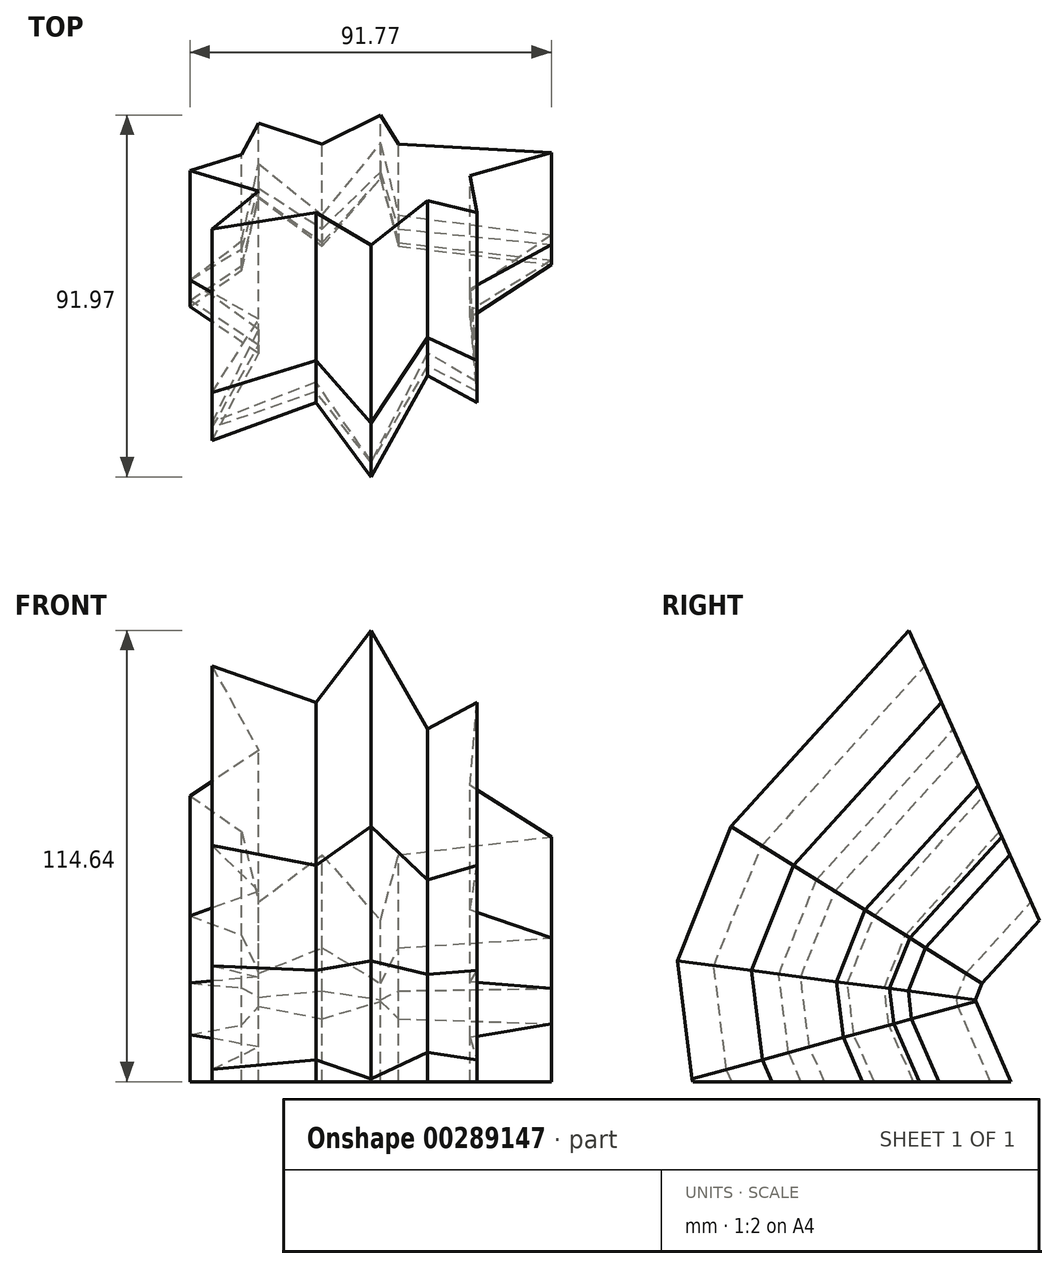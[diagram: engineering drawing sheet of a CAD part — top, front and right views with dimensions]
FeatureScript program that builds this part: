
annotation { "Feature Type Name" : "Feature", "Feature Type Description" : "" }
export const myFeature = defineFeature(function(context is Context, id is Id, definition is map)
    precondition{}
    {
        {
            var Q0;
            Q0=qCreatedBy(makeId("Top.planeOp"),FACE);
            var sketch = newSketch(context, id + "F0", { "sketchPlane" : qUnion([Q0])});
            skLineSegment(sketch, "E0", {"start": v(-44, 0) * mm, "end": v(-30.89, 9.97) * mm});
            skLineSegment(sketch, "E1", {"start": v(-30.89, 9.97) * mm, "end": v(-26.58, 29.54) * mm});
            skLineSegment(sketch, "E2", {"start": v(-26.58, 29.54) * mm, "end": v(-10.42, 16.43) * mm});
            skLineSegment(sketch, "E3", {"start": v(-10.42, 16.43) * mm, "end": v(4.37, 34.67) * mm});
            skLineSegment(sketch, "E4", {"start": v(4.37, 34.67) * mm, "end": v(8.98, 16.43) * mm});
            skLineSegment(sketch, "E5", {"start": v(8.98, 16.43) * mm, "end": v(47.77, 11.4) * mm});
            skLineSegment(sketch, "E6", {"start": v(47.77, 11.4) * mm, "end": v(27.12, -2.96) * mm});
            skLineSegment(sketch, "E7", {"start": v(27.12, -2.96) * mm, "end": v(28.91, -25.95) * mm});
            skLineSegment(sketch, "E8", {"start": v(28.91, -25.95) * mm, "end": v(16.34, -18.59) * mm});
            skLineSegment(sketch, "E9", {"start": v(16.34, -18.59) * mm, "end": v(1.98, -46.06) * mm});
            skLineSegment(sketch, "E10", {"start": v(1.98, -46.06) * mm, "end": v(-12.03, -25.95) * mm});
            skLineSegment(sketch, "E11", {"start": v(-12.03, -25.95) * mm, "end": v(-38.43, -36.19) * mm});
            skLineSegment(sketch, "E12", {"start": v(-38.43, -36.19) * mm, "end": v(-26.58, -12.66) * mm});
            skLineSegment(sketch, "E13", {"start": v(-26.58, -12.66) * mm, "end": v(-44, 0) * mm});
            skSolve(sketch);
        }
        {
            var Q0;
            Q0=qCreatedBy(makeId("Right.planeOp"),FACE);
            var sketch = newSketch(context, id + "F1", { "sketchPlane" : qUnion([Q0])});
            skLineSegment(sketch, "E14", {"start": v(0, 0) * mm, "end": v(-5.2, 11.94) * mm});
            skLineSegment(sketch, "E15", {"start": v(-5.2, 11.94) * mm, "end": v(-6.82, 25.05) * mm});
            skLineSegment(sketch, "E16", {"start": v(-6.82, 25.05) * mm, "end": v(0, 42.11) * mm});
            skLineSegment(sketch, "E17", {"start": v(0, 42.11) * mm, "end": v(24.96, 69.6) * mm});
            skLineSegment(sketch, "E18", {"start": v(24.96, 69.6) * mm, "end": v(27.7, 72.61) * mm});
            skSolve(sketch);
        }
        {
            var Q0;
            Q0=makeQuery(id+"F0.imprint","IMPRINT",FACE,{"disambiguationData":[TD([[makeQuery(id+"F0.imprint","IMPRINT",EDGE,{"derivedFrom":sQuery(id+"F0.wireOp",EDGE,"E0")}),-1.0]])]});
            var Q1;
            Q1=sQuery(id+"F1.wireOp",EDGE,"E14");
            var Q2;
            Q2=sQuery(id+"F1.wireOp",EDGE,"E17");
            var Q3;
            Q3=sQuery(id+"F1.wireOp",EDGE,"E15");
            var Q4;
            Q4=sQuery(id+"F1.wireOp",EDGE,"E16");
            var Q5;
            Q5=sQuery(id+"F1.wireOp",EDGE,"E18");
            sweep(context, id + "F2", {"profiles" : qUnion([Q0]), "path" : qUnion([Q1, Q2, Q3, Q4, Q5])});
        }
    });
